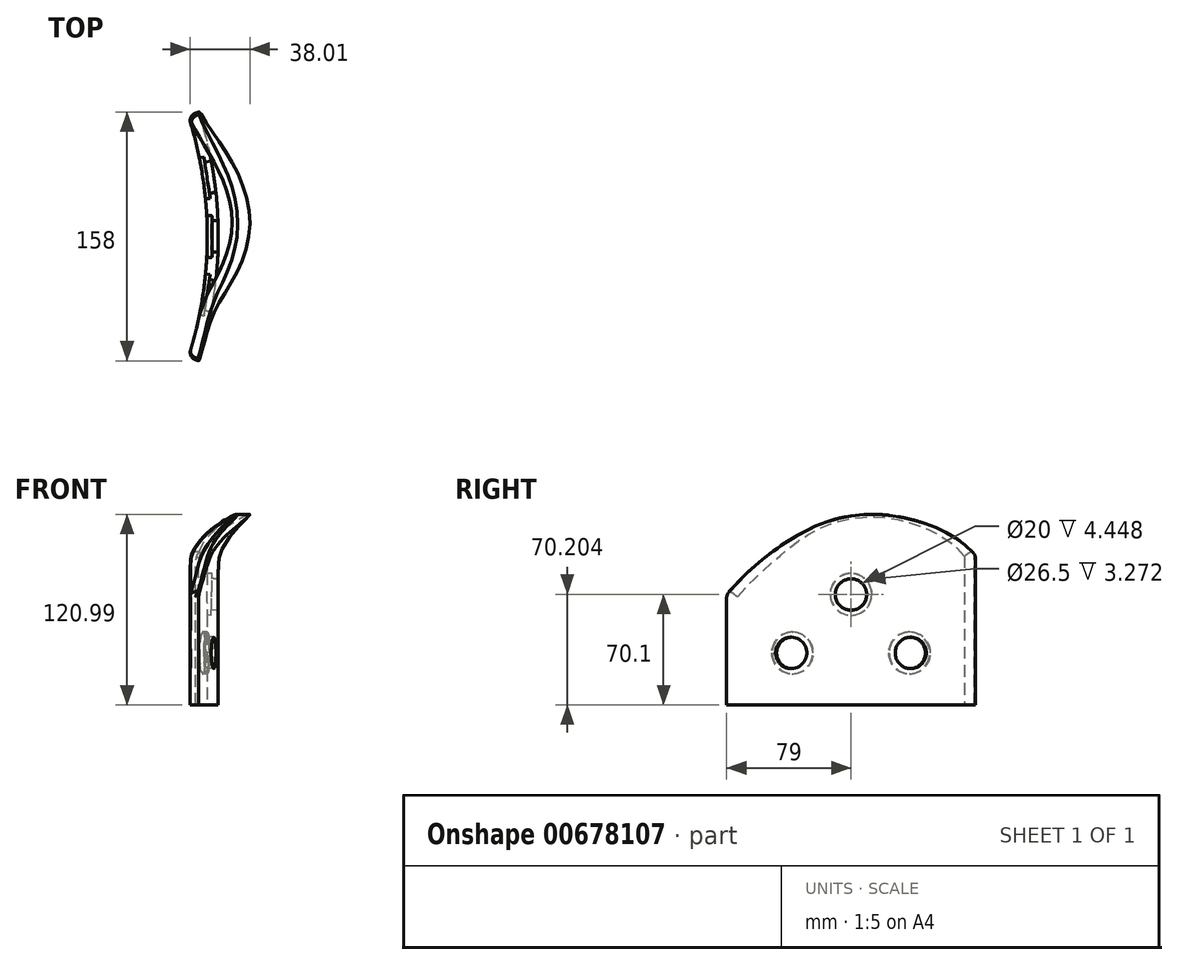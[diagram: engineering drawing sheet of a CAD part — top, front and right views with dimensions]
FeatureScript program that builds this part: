
annotation { "Feature Type Name" : "Feature", "Feature Type Description" : "" }
export const myFeature = defineFeature(function(context is Context, id is Id, definition is map)
    precondition{}
    {
        {
            var Q0;
            Q0=qCreatedBy(makeId("Top.planeOp"),FACE);
            var sketch = newSketch(context, id + "F0", { "sketchPlane" : qUnion([Q0])});
            skCircle(sketch, "E0", {"center": v(0, 0) * mm, "radius": 250 * mm});
            skCircle(sketch, "E1", {"center": v(0, 0) * mm, "radius": 257 * mm});
            skLineSegment(sketch, "E2", {"start": v(0, 0) * mm, "end": v(244.56, 79) * mm});
            skLineSegment(sketch, "E3", {"start": v(0, 0) * mm, "end": v(244.56, -79) * mm});
            skLineSegment(sketch, "E4", {"start": v(244.56, -79) * mm, "end": v(244.56, 79) * mm, "construction": true});
            skPoint(sketch, "E5", {"position": v(250, 0) * mm});
            skLineSegment(sketch, "E6", {"start": v(0, 0) * mm, "end": v(295.52, 0) * mm, "construction": true});
            skPoint(sketch, "E6.endSnap0", {"position": v(244.56, 0) * mm});
            skLineSegment(sketch, "E7", {"start": v(0, 0) * mm, "end": v(293.26, 43.83) * mm, "construction": true});
            skLineSegment(sketch, "E8", {"start": v(0, 0) * mm, "end": v(282.96, -42.29) * mm, "construction": true});
            skSolve(sketch);
        }
        {
            var Q0;
            Q0=qCreatedBy(makeId("Front.planeOp"),FACE);
            var sketch = newSketch(context, id + "F1", { "sketchPlane" : qUnion([Q0])});
            skLineSegment(sketch, "E9.0", {"start": v(-250, 0) * mm, "end": v(250, 0) * mm, "construction": true});
            skLineSegment(sketch, "E10.0", {"start": v(-257, 0) * mm, "end": v(257, 0) * mm, "construction": true});
            skPoint(sketch, "E11.0", {"position": v(244.56, 0) * mm});
            skLineSegment(sketch, "E12", {"start": v(250, 0) * mm, "end": v(257, 0) * mm, "construction": true});
            skPoint(sketch, "E13", {"position": v(253.5, 0) * mm});
            skFitSpline(sketch, "E14", {"points": [v(253.5, 0) * mm, v(253.5, 82.58) * mm, v(278.5, 127) * mm], "startDerivative": vector(0, 188.26) * mm, "endDerivative": vector(170.46, 163.73) * mm});
            skLineSegment(sketch, "E15", {"start": v(253.5, 0) * mm, "end": v(253.5, 133.7) * mm, "construction": true});
            skSolve(sketch);
        }
        {
            var Q0;
            {var subQ0=sQuery(id+"F0.wireOp",EDGE,"E2");var subQ1=sQuery(id+"F0.wireOp",EDGE,"E0");var subQ2=makeQuery(id+"F0.imprint","INTERSECT",VERTEX,{"derivedFrom":[subQ1,subQ0]});Q0=makeQuery(id+"F0.imprint","IMPRINT",FACE,{"disambiguationData":[TD([[makeQuery(id+"F0.imprint","IMPRINT",EDGE,{"disambiguationData":[TD([[subQ2,1.0]])],"derivedFrom":subQ1}),-1.0]])]});}
            var Q1;
            Q1=sQuery(id+"F1.wireOp",EDGE,"E14");
            sweep(context, id + "F2", {"profiles" : qUnion([Q0]), "path" : qUnion([Q1])});
        }
        {
            var Q0;
            Q0=makeQuery(id+"F2.opSweep","SWEPT_EDGE",EDGE,{"disambiguationData":[OSD([sQuery(id+"F0.wireOp",EDGE,"E1"),sQuery(id+"F0.wireOp",EDGE,"E3"),sQuery(id+"F1.wireOp",EDGE,"E14")])]});
            cPoint(context, id + "F3", {"entities" : qUnion([Q0]), "parameter" : 0.5});
        }
        {
            var Q0;
            Q0=qCreatedBy(makeId("Front.planeOp"),FACE);
            var Q1;
            Q1=qCreatedBy(id+"F3",VERTEX);
            cPlane(context, id + "F4", {"entities" : qUnion([Q0, Q1]), "cplaneType" : CPlaneType.PLANE_POINT, "offset" : 25 * mm, "width" : 150 * mm, "height" : 150 * mm});
        }
        {
            var Q0;
            Q0=qCreatedBy(id+"F4.planeOp",FACE);
            var sketch = newSketch(context, id + "F5", { "sketchPlane" : qUnion([Q0])});
            skLineSegment(sketch, "E16", {"start": v(16.14, 70) * mm, "end": v(342.74, 70) * mm});
            skLineSegment(sketch, "E17.top", {"start": v(16.14, 220) * mm, "end": v(342.74, 220) * mm});
            skLineSegment(sketch, "E17.left", {"start": v(16.14, 70) * mm, "end": v(16.14, 220) * mm});
            skLineSegment(sketch, "E17.right", {"start": v(342.74, 70) * mm, "end": v(342.74, 220) * mm});
            skSolve(sketch);
        }
        {
            var Q0;
            Q0=qCreatedBy(makeId("Right.planeOp"),FACE);
            var sketch = newSketch(context, id + "F6", { "sketchPlane" : qUnion([Q0])});
            skPoint(sketch, "E18.0", {"position": v(-79, 70) * mm});
            skLineSegment(sketch, "E19", {"start": v(-74, 70) * mm, "end": v(-141.5, 70) * mm, "construction": true});
            skFitSpline(sketch, "E20.0", {"points": [v(74, 0) * mm, v(1000, 74) * mm, v(25.09, 1000) * mm, v(74, 37.34) * mm, v(1000, 74) * mm, v(48.67, 1000) * mm, v(74, 51.29) * mm, v(1000, 74) * mm, v(56.25, 1000) * mm, v(74, 58.58) * mm, v(1000, 74) * mm, v(63.15, 1000) * mm, v(74, 64.9) * mm, v(1000, 74) * mm, v(68.8, 1000) * mm, v(74, 70.94) * mm, v(1000, 74) * mm, v(77.76, 1000) * mm], "construction": true});
            skFitSpline(sketch, "E21.0", {"points": [v(-74, 0) * mm, v(1000, -74) * mm, v(25.09, 1000) * mm, v(-74, 37.34) * mm, v(1000, -74) * mm, v(48.67, 1000) * mm, v(-74, 51.29) * mm, v(1000, -74) * mm, v(56.25, 1000) * mm, v(-74, 58.58) * mm, v(1000, -74) * mm, v(63.15, 1000) * mm, v(-74, 64.9) * mm, v(1000, -74) * mm, v(68.8, 1000) * mm, v(-74, 70.94) * mm, v(1000, -74) * mm, v(77.76, 1000) * mm], "construction": true});
            skLineSegment(sketch, "E22", {"start": v(68.45, 95) * mm, "end": v(-5.43, 95) * mm, "construction": true});
            skLineSegment(sketch, "E23", {"start": v(28.07, 120) * mm, "end": v(-24.08, 120) * mm, "construction": true});
            skFitSpline(sketch, "E24", {"points": [v(79, 95) * mm, v(37.6, 117.94) * mm, v(0, 120) * mm, v(-31.96, 108.87) * mm, v(-79, 70) * mm], "startDerivative": vector(-101.15, 130.6) * mm, "endDerivative": vector(-145.98, -173.37) * mm});
            skSolve(sketch);
        }
        {
            var Q0;
            Q0=makeQuery(id+"F5.imprint","IMPRINT",FACE,{"disambiguationData":[TD([[makeQuery(id+"F5.imprint","IMPRINT",EDGE,{"derivedFrom":sQuery(id+"F5.wireOp",EDGE,"E16")}),1.0]])]});
            var Q1;
            Q1=sQuery(id+"F6.wireOp",EDGE,"E24");
            sweep(context, id + "F7", {"operationType" : NewBodyOperationType.REMOVE, "profiles" : qUnion([Q0]), "path" : qUnion([Q1]), "keepProfileOrientation" : true});
        }
        {
            var Q0;
            Q0=makeQuery(id+"F7.boolean.opBoolean","INTERSECT",EDGE,{"derivedFrom":[makeQuery(id+"F2.opSweep","SWEPT_FACE",FACE,{"disambiguationData":[OSD([sQuery(id+"F0.wireOp",EDGE,"E0"),sQuery(id+"F1.wireOp",EDGE,"E14")])]}),makeQuery(id+"F7.opSweep","SWEPT_FACE",FACE,{"disambiguationData":[OSD([sQuery(id+"F5.wireOp",EDGE,"E16"),sQuery(id+"F6.wireOp",EDGE,"E24")])]})]});
            fillet(context, id + "F8", {"entities" : qUnion([Q0]), "radius" : 5 * mm, "tangentPropagation" : true, "allowEdgeOverflow" : false});
        }
        {
            var Q0;
            Q0=makeQuery(id+"F2.opSweep","SWEPT_EDGE",EDGE,{"disambiguationData":[OSD([sQuery(id+"F0.wireOp",EDGE,"E0"),sQuery(id+"F0.wireOp",EDGE,"E2"),sQuery(id+"F1.wireOp",EDGE,"E14")])]});
            var Q1;
            Q1=makeQuery(id+"F2.opSweep","SWEPT_EDGE",EDGE,{"disambiguationData":[OSD([sQuery(id+"F0.wireOp",EDGE,"E0"),sQuery(id+"F0.wireOp",EDGE,"E3"),sQuery(id+"F1.wireOp",EDGE,"E14")])]});
            fillet(context, id + "F9", {"entities" : qUnion([Q0, Q1]), "radius" : 5 * mm, "tangentPropagation" : true, "allowEdgeOverflow" : false});
        }
        {
            var Q0;
            Q0=qCreatedBy(makeId("Front.planeOp"),FACE);
            var sketch = newSketch(context, id + "F10", { "sketchPlane" : qUnion([Q0])});
            skLineSegment(sketch, "E25", {"start": v(0, 0) * mm, "end": v(178.06, -4.84) * mm, "construction": true});
            skSolve(sketch);
        }
        {
            var Q0;
            Q0=sQuery(id+"F0.wireOp",VERTEX,"E2.start");
            var Q1;
            Q1=sQuery(id+"F10.wireOp",EDGE,"E25");
            cPlane(context, id + "F11", {"entities" : qUnion([Q0, Q1]), "cplaneType" : CPlaneType.LINE_POINT, "offset" : 0 * mm, "width" : 150 * mm, "height" : 150 * mm});
        }
        {
            var Q0;
            Q0=sQuery(id+"F0.wireOp",EDGE,"E7");
            var Q1;
            Q1=sQuery(id+"F0.wireOp",VERTEX,"E2.start");
            cPlane(context, id + "F12", {"entities" : qUnion([Q0, Q1]), "cplaneType" : CPlaneType.LINE_POINT, "offset" : 25 * mm, "width" : 150 * mm, "height" : 150 * mm});
        }
        {
            var Q0;
            Q0=sQuery(id+"F0.wireOp",VERTEX,"E2.start");
            var Q1;
            Q1=sQuery(id+"F0.wireOp",EDGE,"E8");
            cPlane(context, id + "F13", {"entities" : qUnion([Q0, Q1]), "cplaneType" : CPlaneType.LINE_POINT, "offset" : 25 * mm, "width" : 150 * mm, "height" : 150 * mm});
        }
        {
            var Q0;
            Q0=qCreatedBy(id+"F12.planeOp",FACE);
            var sketch = newSketch(context, id + "F14", { "sketchPlane" : qUnion([Q0])});
            skCircle(sketch, "E26", {"center": v(0, 33) * mm, "radius": 10 * mm});
            skCircle(sketch, "E27", {"center": v(0, 33) * mm, "radius": 13.25 * mm});
            skLineSegment(sketch, "E28", {"start": v(0, 0) * mm, "end": v(0, 72.86) * mm, "construction": true});
            skLineSegment(sketch, "E29", {"start": v(-106.85, 69.08) * mm, "end": v(48.95, 69.08) * mm, "construction": true});
            skSolve(sketch);
        }
        {
            var Q0;
            Q0=qCreatedBy(id+"F13.planeOp",FACE);
            var sketch = newSketch(context, id + "F15", { "sketchPlane" : qUnion([Q0])});
            skCircle(sketch, "E30", {"center": v(-0.04, 33) * mm, "radius": 10 * mm});
            skCircle(sketch, "E31", {"center": v(-0.04, 33) * mm, "radius": 13.25 * mm});
            skLineSegment(sketch, "E32", {"start": v(0, 0) * mm, "end": v(0, 72.55) * mm, "construction": true});
            skLineSegment(sketch, "E33", {"start": v(-35.94, 69.08) * mm, "end": v(109.12, 69.08) * mm, "construction": true});
            skSolve(sketch);
        }
        {
            var Q0;
            Q0=qCreatedBy(id+"F11.planeOp",FACE);
            var sketch = newSketch(context, id + "F16", { "sketchPlane" : qUnion([Q0])});
            skLineSegment(sketch, "E34", {"start": v(0, 0) * mm, "end": v(0, 92.68) * mm, "construction": true});
            skCircle(sketch, "E35", {"center": v(0, 77) * mm, "radius": 10 * mm});
            skCircle(sketch, "E36", {"center": v(0, 77) * mm, "radius": 13.25 * mm});
            skSolve(sketch);
        }
        {
            var Q0;
            Q0=makeQuery(id+"F14.imprint","IMPRINT",FACE,{"disambiguationData":[TD([[makeQuery(id+"F14.imprint","IMPRINT",EDGE,{"derivedFrom":sQuery(id+"F14.wireOp",EDGE,"E26")}),1.0]])]});
            extrude(context, id + "F17", {"entities" : qUnion([Q0]), "operationType" : NewBodyOperationType.REMOVE, "depth" : 260 * mm, "offsetDistance" : 25 * mm});
        }
        {
            var Q0;
            Q0=makeQuery(id+"F15.imprint","IMPRINT",FACE,{"disambiguationData":[TD([[makeQuery(id+"F15.imprint","IMPRINT",EDGE,{"derivedFrom":sQuery(id+"F15.wireOp",EDGE,"E30")}),1.0]])]});
            extrude(context, id + "F18", {"entities" : qUnion([Q0]), "operationType" : NewBodyOperationType.REMOVE, "depth" : 260 * mm, "offsetDistance" : 25 * mm});
        }
        {
            var Q0;
            Q0=makeQuery(id+"F16.imprint","IMPRINT",FACE,{"disambiguationData":[TD([[makeQuery(id+"F16.imprint","IMPRINT",EDGE,{"derivedFrom":sQuery(id+"F16.wireOp",EDGE,"E35")}),1.0]])]});
            extrude(context, id + "F19", {"entities" : qUnion([Q0]), "operationType" : NewBodyOperationType.REMOVE, "depth" : 260 * mm, "offsetDistance" : 25 * mm});
        }
        {
            var Q0;
            Q0=makeQuery(id+"F15.imprint","IMPRINT",FACE,{"disambiguationData":[TD([[makeQuery(id+"F15.imprint","IMPRINT",EDGE,{"derivedFrom":sQuery(id+"F15.wireOp",EDGE,"E30")}),-1.0]])]});
            extrude(context, id + "F20", {"entities" : qUnion([Q0]), "operationType" : NewBodyOperationType.REMOVE, "depth" : (249.62 + 3) * mm, "offsetDistance" : 25 * mm});
        }
        {
            var Q0;
            Q0=makeQuery(id+"F16.imprint","IMPRINT",FACE,{"disambiguationData":[TD([[makeQuery(id+"F16.imprint","IMPRINT",EDGE,{"derivedFrom":sQuery(id+"F16.wireOp",EDGE,"E35")}),-1.0]])]});
            extrude(context, id + "F21", {"entities" : qUnion([Q0]), "operationType" : NewBodyOperationType.REMOVE, "depth" : (248.03 + 2.8) * mm, "offsetDistance" : 25 * mm});
        }
        {
            var Q0;
            Q0=makeQuery(id+"F14.imprint","IMPRINT",FACE,{"disambiguationData":[TD([[makeQuery(id+"F14.imprint","IMPRINT",EDGE,{"derivedFrom":sQuery(id+"F14.wireOp",EDGE,"E26")}),-1.0]])]});
            extrude(context, id + "F22", {"entities" : qUnion([Q0]), "operationType" : NewBodyOperationType.REMOVE, "depth" : (249.62 + 3) * mm, "offsetDistance" : 25 * mm});
        }
    });
